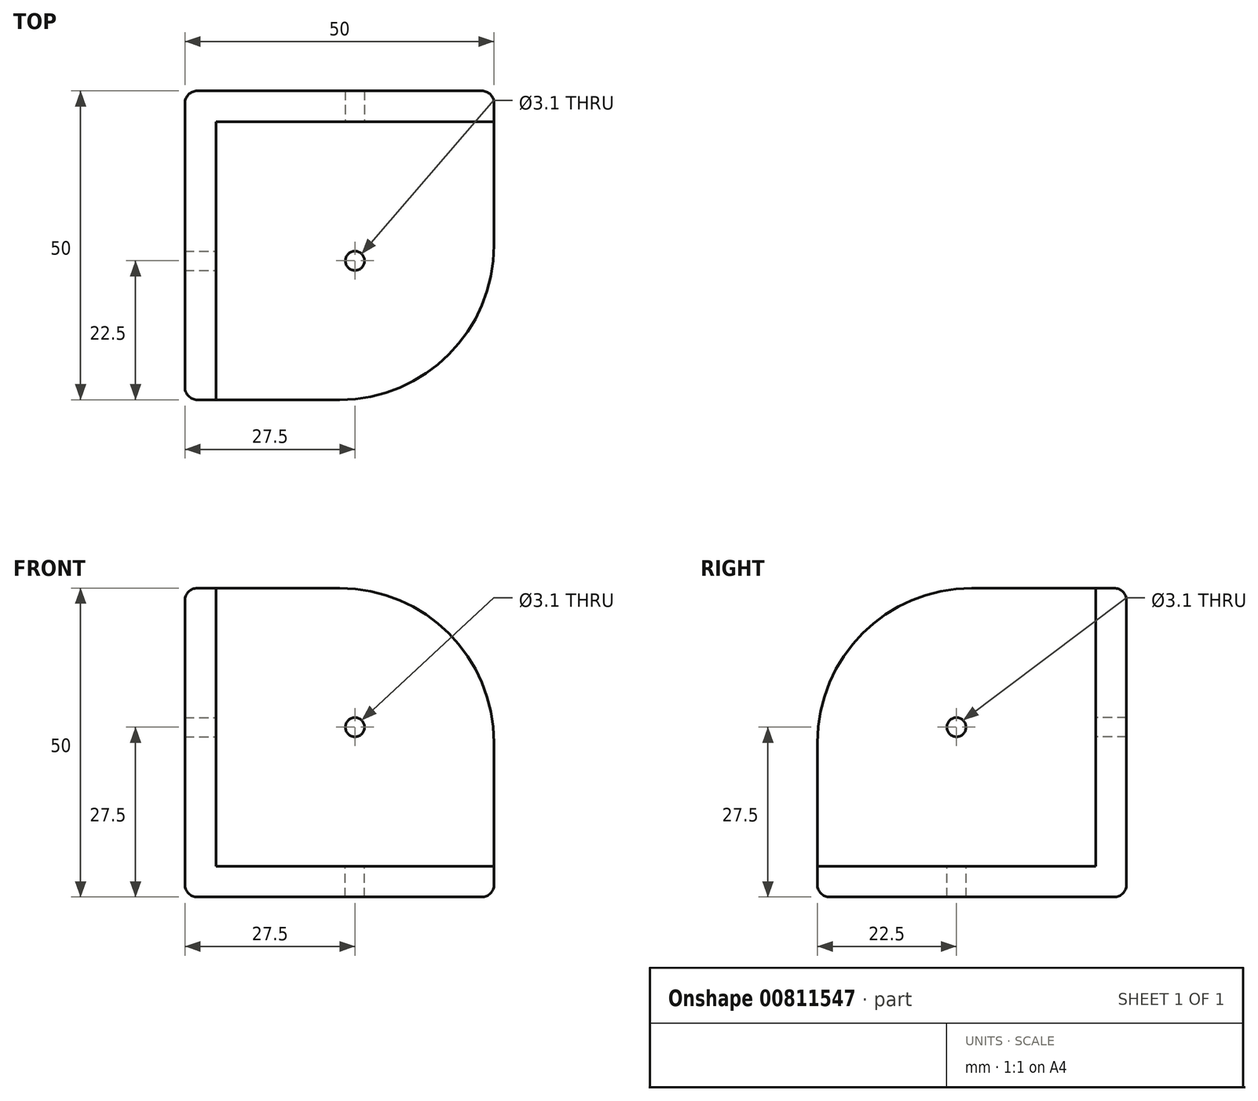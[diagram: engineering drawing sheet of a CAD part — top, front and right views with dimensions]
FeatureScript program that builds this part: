
annotation { "Feature Type Name" : "Feature", "Feature Type Description" : "" }
export const myFeature = defineFeature(function(context is Context, id is Id, definition is map)
    precondition{}
    {
        {
            var Q0;
            Q0=qCreatedBy(makeId("Top.planeOp"),FACE);
            var sketch = newSketch(context, id + "F0", { "sketchPlane" : qUnion([Q0])});
            skLineSegment(sketch, "E0.bottom", {"start": v(25, -25) * mm, "end": v(-25, -25) * mm});
            skLineSegment(sketch, "E0.top", {"start": v(25, 25) * mm, "end": v(-25, 25) * mm});
            skLineSegment(sketch, "E0.left", {"start": v(25, -25) * mm, "end": v(25, 25) * mm});
            skLineSegment(sketch, "E0.right", {"start": v(-25, -25) * mm, "end": v(-25, 25) * mm});
            skPoint(sketch, "E0.middle", {"position": v(0, 0) * mm});
            skSolve(sketch);
        }
        {
            var Q0;
            Q0=makeQuery(id+"F0.imprint","IMPRINT",FACE,{"disambiguationData":[TD([[makeQuery(id+"F0.imprint","IMPRINT",EDGE,{"derivedFrom":sQuery(id+"F0.wireOp",EDGE,"E0.bottom")}),-1.0]])]});
            extrude(context, id + "F1", {"entities" : qUnion([Q0]), "depth" : 5 * mm, "offsetDistance" : 25 * mm});
        }
        {
            var Q0;
            Q0=makeQuery(id+"F1.opExtrude","CAP_FACE",FACE,{"disambiguationData":[OSD([sQuery(id+"F0.wireOp",EDGE,"E0.bottom"),sQuery(id+"F0.wireOp",EDGE,"E0.top"),sQuery(id+"F0.wireOp",EDGE,"E0.left"),sQuery(id+"F0.wireOp",EDGE,"E0.right")])],"isStart":false});
            var sketch = newSketch(context, id + "F2", { "sketchPlane" : qUnion([Q0])});
            skLineSegment(sketch, "E1.bottom", {"start": v(-25, 25) * mm, "end": v(-20, 25) * mm});
            skLineSegment(sketch, "E1.top", {"start": v(-25, -25) * mm, "end": v(-20, -25) * mm});
            skLineSegment(sketch, "E1.left", {"start": v(-25, 25) * mm, "end": v(-25, -25) * mm});
            skLineSegment(sketch, "E1.right", {"start": v(-20, 25) * mm, "end": v(-20, -25) * mm});
            skLineSegment(sketch, "E2.bottom", {"start": v(-20, 25) * mm, "end": v(25, 25) * mm});
            skLineSegment(sketch, "E2.top", {"start": v(-20, 20) * mm, "end": v(25, 20) * mm});
            skLineSegment(sketch, "E2.left", {"start": v(-20, 25) * mm, "end": v(-20, 20) * mm});
            skLineSegment(sketch, "E2.right", {"start": v(25, 25) * mm, "end": v(25, 20) * mm});
            skSolve(sketch);
        }
        {
            var Q0;
            Q0=qSketchRegion(id+"F2",true);
            extrude(context, id + "F3", {"entities" : qUnion([Q0]), "operationType" : NewBodyOperationType.ADD, "depth" : 45 * mm, "offsetDistance" : 25 * mm});
        }
        {
            var Q0;
            Q0=makeQuery(id+"F3.opExtrude","CAP_EDGE",EDGE,{"disambiguationData":[OSD([sQuery(id+"F2.wireOp",EDGE,"E2.right")])],"isStart":false});
            var Q1;
            Q1=makeQuery(id+"F3.opExtrude","CAP_EDGE",EDGE,{"disambiguationData":[OSD([sQuery(id+"F2.wireOp",EDGE,"E1.top")])],"isStart":false});
            var Q2;
            Q2=makeQuery(id+"F1.opExtrude","SWEPT_EDGE",EDGE,{"disambiguationData":[OSD([sQuery(id+"F0.wireOp",EDGE,"E0.bottom"),sQuery(id+"F0.wireOp",EDGE,"E0.left")])]});
            fillet(context, id + "F4", {"entities" : qUnion([Q0, Q1, Q2]), "radius" : 25 * mm, "tangentPropagation" : true, "allowEdgeOverflow" : false});
        }
        {
            var Q0;
            Q0=makeQuery(id+"F1.opExtrude","CAP_FACE",FACE,{"disambiguationData":[OSD([sQuery(id+"F0.wireOp",EDGE,"E0.bottom"),sQuery(id+"F0.wireOp",EDGE,"E0.top"),sQuery(id+"F0.wireOp",EDGE,"E0.left"),sQuery(id+"F0.wireOp",EDGE,"E0.right")])],"isStart":true});
            var Q1;
            Q1=makeQuery(id+"F3.boolean.opBoolean","MERGE",FACE,{"derivedFrom":[makeQuery(id+"F1.opExtrude","SWEPT_FACE",FACE,{"disambiguationData":[OSD([sQuery(id+"F0.wireOp",EDGE,"E0.right")])]}),makeQuery(id+"F3.opExtrude","SWEPT_FACE",FACE,{"disambiguationData":[OSD([sQuery(id+"F2.wireOp",EDGE,"E1.left")])]})]});
            var Q2;
            Q2=makeQuery(id+"F3.boolean.opBoolean","MERGE",FACE,{"derivedFrom":[makeQuery(id+"F1.opExtrude","SWEPT_FACE",FACE,{"disambiguationData":[OSD([sQuery(id+"F0.wireOp",EDGE,"E0.top")])]}),makeQuery(id+"F3.opExtrude","SWEPT_FACE",FACE,{"disambiguationData":[OSD([sQuery(id+"F2.wireOp",EDGE,"E1.bottom"),sQuery(id+"F2.wireOp",EDGE,"E2.bottom")])]})]});
            fillet(context, id + "F5", {"entities" : qUnion([Q0, Q1, Q2]), "radius" : 2 * mm, "tangentPropagation" : true, "allowEdgeOverflow" : false});
        }
        {
            var Q0;
            Q0=makeQuery(id+"F1.opExtrude","CAP_FACE",FACE,{"disambiguationData":[OSD([sQuery(id+"F0.wireOp",EDGE,"E0.bottom"),sQuery(id+"F0.wireOp",EDGE,"E0.top"),sQuery(id+"F0.wireOp",EDGE,"E0.left"),sQuery(id+"F0.wireOp",EDGE,"E0.right")])],"isStart":false});
            var sketch = newSketch(context, id + "F6", { "sketchPlane" : qUnion([Q0])});
            skPoint(sketch, "E3", {"position": v(2.5, -2.5) * mm});
            skPoint(sketch, "E3.positionSnap0", {"position": v(-20, -2.5) * mm});
            skPoint(sketch, "E3.positionSnap1", {"position": v(2.5, 20) * mm});
            skSolve(sketch);
        }
        {
            var Q0;
            Q0=makeQuery(id+"F3.opExtrude","SWEPT_FACE",FACE,{"disambiguationData":[OSD([sQuery(id+"F2.wireOp",EDGE,"E1.right")])]});
            var sketch = newSketch(context, id + "F7", { "sketchPlane" : qUnion([Q0])});
            skPoint(sketch, "E4", {"position": v(-2.5, 27.5) * mm});
            skPoint(sketch, "E4.positionSnap0", {"position": v(20, 27.5) * mm});
            skPoint(sketch, "E4.positionSnap1", {"position": v(-2.5, 5) * mm});
            skSolve(sketch);
        }
        {
            var Q0;
            Q0=makeQuery(id+"F3.opExtrude","SWEPT_FACE",FACE,{"disambiguationData":[OSD([sQuery(id+"F2.wireOp",EDGE,"E2.top")])]});
            var sketch = newSketch(context, id + "F8", { "sketchPlane" : qUnion([Q0])});
            skPoint(sketch, "E5", {"position": v(2.5, 27.5) * mm});
            skPoint(sketch, "E5.positionSnap0", {"position": v(2.5, 5) * mm});
            skPoint(sketch, "E5.positionSnap1", {"position": v(-20, 27.5) * mm});
            skSolve(sketch);
        }
        {
            var Q0;
            Q0=sQuery(id+"F7.wireOp",VERTEX,"E4");
            var Q1;
            Q1=sQuery(id+"F6.wireOp",VERTEX,"E3");
            var Q2;
            Q2=sQuery(id+"F8.wireOp",VERTEX,"E5");
            var Q3;
            Q3=makeQuery(id+"F1.opExtrude","SWEPT_BODY",BODY,{"disambiguationData":[OSD([sQuery(id+"F0.wireOp",EDGE,"E0.bottom"),sQuery(id+"F0.wireOp",EDGE,"E0.top"),sQuery(id+"F0.wireOp",EDGE,"E0.left"),sQuery(id+"F0.wireOp",EDGE,"E0.right")])]});
            hole(context, id + "F9", {"style" : HoleStyle.SIMPLE, "endStyle" : HoleEndStyle.BLIND, "holeDiameter" : 3.1 * mm, "majorDiameter" : 5 * mm, "holeDepth" : 20 * mm, "isTappedThrough" : true, "tappedDepth" : 12 * mm, "tapClearance" : 3, "locations" : qUnion([Q0, Q1, Q2]), "scope" : qUnion([Q3])});
        }
    });
